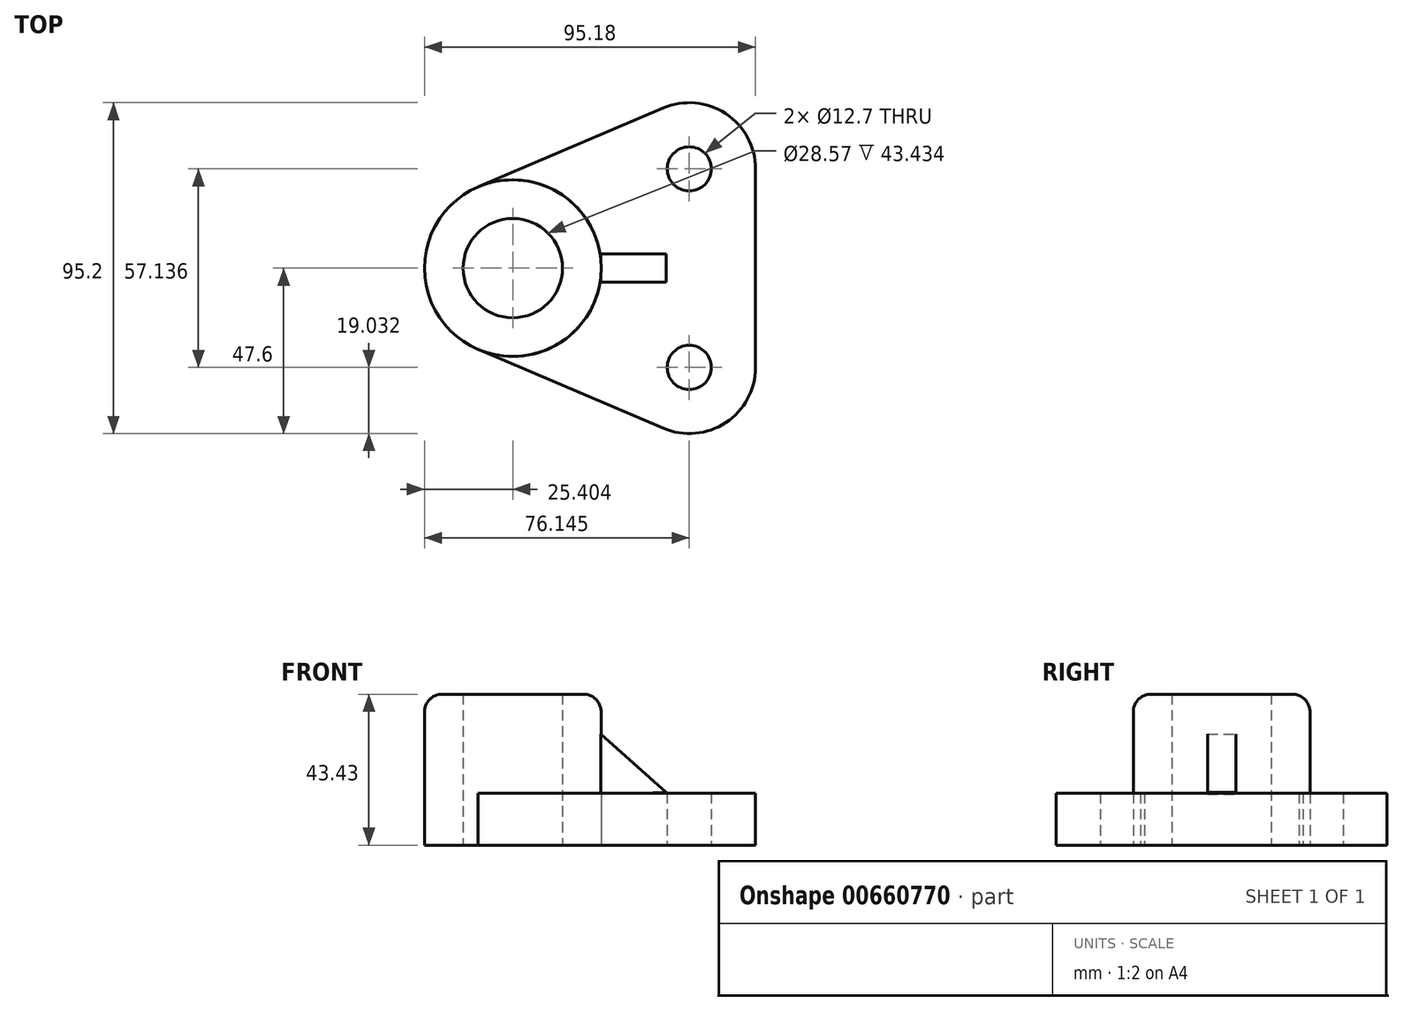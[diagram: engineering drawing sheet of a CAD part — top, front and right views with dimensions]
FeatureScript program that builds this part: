
annotation { "Feature Type Name" : "Feature", "Feature Type Description" : "" }
export const myFeature = defineFeature(function(context is Context, id is Id, definition is map)
    precondition{}
    {
        {
            var Q0;
            Q0=qCreatedBy(makeId("Top.planeOp"),FACE);
            var sketch = newSketch(context, id + "F0", { "sketchPlane" : qUnion([Q0])});
            skCircle(sketch, "E0", {"center": v(-37.52, 0) * mm, "radius": 14.29 * mm});
            skCircle(sketch, "E1", {"center": v(13.22, 28.57) * mm, "radius": 6.35 * mm});
            skCircle(sketch, "E2", {"center": v(13.22, -28.57) * mm, "radius": 6.35 * mm});
            skArc(sketch, "E3", {"start": v(32.26, 28.57) * mm, "mid": v(23.72, 44.45) * mm, "end": v(5.76, 46.07) * mm});
            skArc(sketch, "E4", {"start": v(5.76, -46.07) * mm, "mid": v(23.72, -44.45) * mm, "end": v(32.26, -28.57) * mm});
            skCircle(sketch, "E5", {"center": v(-37.52, 0) * mm, "radius": 25.4 * mm});
            skLineSegment(sketch, "E6", {"start": v(-47.48, 23.36) * mm, "end": v(5.76, 46.07) * mm});
            skLineSegment(sketch, "E7", {"start": v(-47.48, -23.36) * mm, "end": v(5.76, -46.07) * mm});
            skLineSegment(sketch, "E8", {"start": v(32.26, 28.57) * mm, "end": v(32.26, -28.57) * mm});
            skSolve(sketch);
        }
        {
            var Q0;
            Q0=makeQuery(id+"F0.imprint","IMPRINT",FACE,{"disambiguationData":[TD([[makeQuery(id+"F0.imprint","IMPRINT",EDGE,{"derivedFrom":sQuery(id+"F0.wireOp",EDGE,"E0")}),-1.0]])]});
            extrude(context, id + "F1", {"entities" : qUnion([Q0]), "depth" : 43.43 * mm, "offsetDistance" : 25.4 * mm});
        }
        {
            var Q0;
            Q0=makeQuery(id+"F0.imprint","IMPRINT",FACE,{"disambiguationData":[TD([[makeQuery(id+"F0.imprint","IMPRINT",EDGE,{"derivedFrom":sQuery(id+"F0.wireOp",EDGE,"E1")}),-1.0]])]});
            var sketch = newSketch(context, id + "F2", { "sketchPlane" : qUnion([Q0])});
            skSolve(sketch);
        }
        {
            var Q0;
            Q0 = qSketchRegion(id + "F2", true);
            var Q1;
            Q1=makeQuery(id+"F0.imprint","IMPRINT",FACE,{"disambiguationData":[TD([[makeQuery(id+"F0.imprint","IMPRINT",EDGE,{"derivedFrom":sQuery(id+"F0.wireOp",EDGE,"E1")}),-1.0]])]});
            extrude(context, id + "F3", {"entities" : qUnion([Q0, Q1]), "depth" : 15 * mm, "offsetDistance" : 25.4 * mm});
        }
        {
            var Q0;
            Q0=qCreatedBy(makeId("Front.planeOp"),FACE);
            var sketch = newSketch(context, id + "F4", { "sketchPlane" : qUnion([Q0])});
            skLineSegment(sketch, "E9", {"start": v(6.54, 15.2) * mm, "end": v(-12.26, 31.99) * mm});
            skLineSegment(sketch, "E10", {"start": v(-12.26, 31.99) * mm, "end": v(-12.26, 14.66) * mm});
            skLineSegment(sketch, "E11", {"start": v(-12.26, 14.66) * mm, "end": v(6.54, 15.2) * mm});
            skSolve(sketch);
        }
        {
            var Q0;
            Q0 = qSketchRegion(id + "F4", true);
            extrude(context, id + "F5", {"entities" : qUnion([Q0]), "endBound" : BoundingType.SYMMETRIC, "depth" : 8.13 * mm, "offsetDistance" : 25.4 * mm});
        }
        {
            var Q0;
            Q0=makeQuery(id+"F1.opExtrude","CAP_EDGE",EDGE,{"disambiguationData":[OSD([sQuery(id+"F0.wireOp",EDGE,"E5")])],"isStart":false});
            fillet(context, id + "F6", {"entities" : qUnion([Q0]), "radius" : 5.08 * mm, "tangentPropagation" : true, "allowEdgeOverflow" : false});
        }
    });
